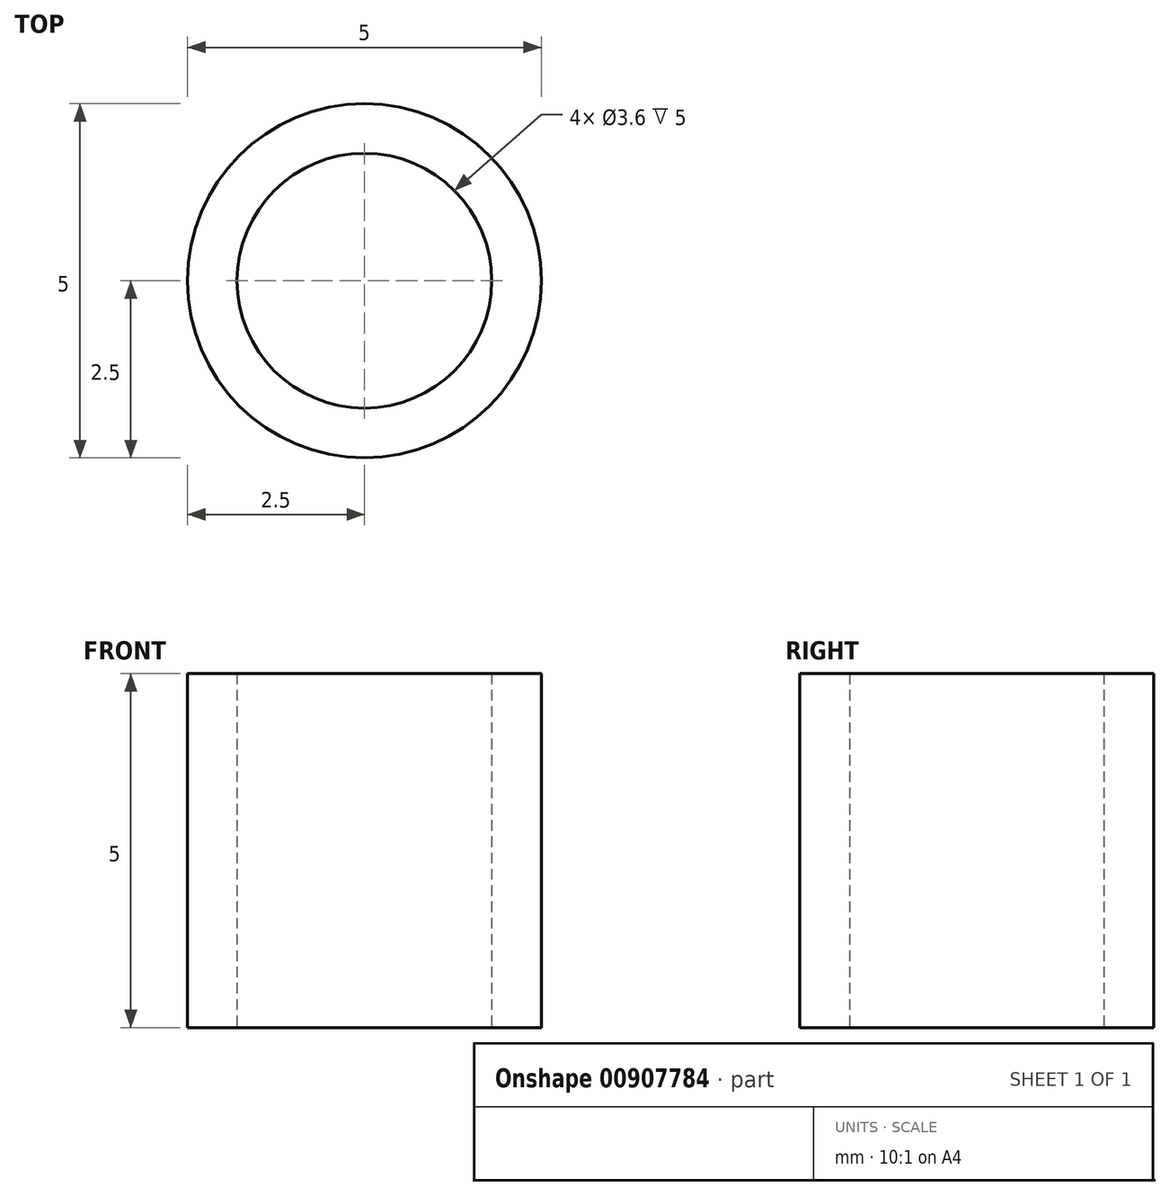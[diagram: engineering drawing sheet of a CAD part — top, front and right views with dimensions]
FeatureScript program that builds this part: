
annotation { "Feature Type Name" : "Feature", "Feature Type Description" : "" }
export const myFeature = defineFeature(function(context is Context, id is Id, definition is map)
    precondition{}
    {
        {
            var Q0;
            Q0=qCreatedBy(makeId("Top.planeOp"),FACE);
            var sketch = newSketch(context, id + "F0", { "sketchPlane" : qUnion([Q0])});
            skCircle(sketch, "E0", {"center": v(0, 0) * mm, "radius": 1.8 * mm});
            skCircle(sketch, "E1", {"center": v(0, 0) * mm, "radius": 2.5 * mm});
            skSolve(sketch);
        }
        {
            var Q0;
            Q0=makeQuery(id+"F0.imprint","IMPRINT",FACE,{"disambiguationData":[TD([[makeQuery(id+"F0.imprint","IMPRINT",EDGE,{"derivedFrom":sQuery(id+"F0.wireOp",EDGE,"E0")}),-1.0]])]});
            extrude(context, id + "F1", {"entities" : qUnion([Q0]), "depth" : 5 * mm, "offsetDistance" : 25 * mm});
        }
    });
